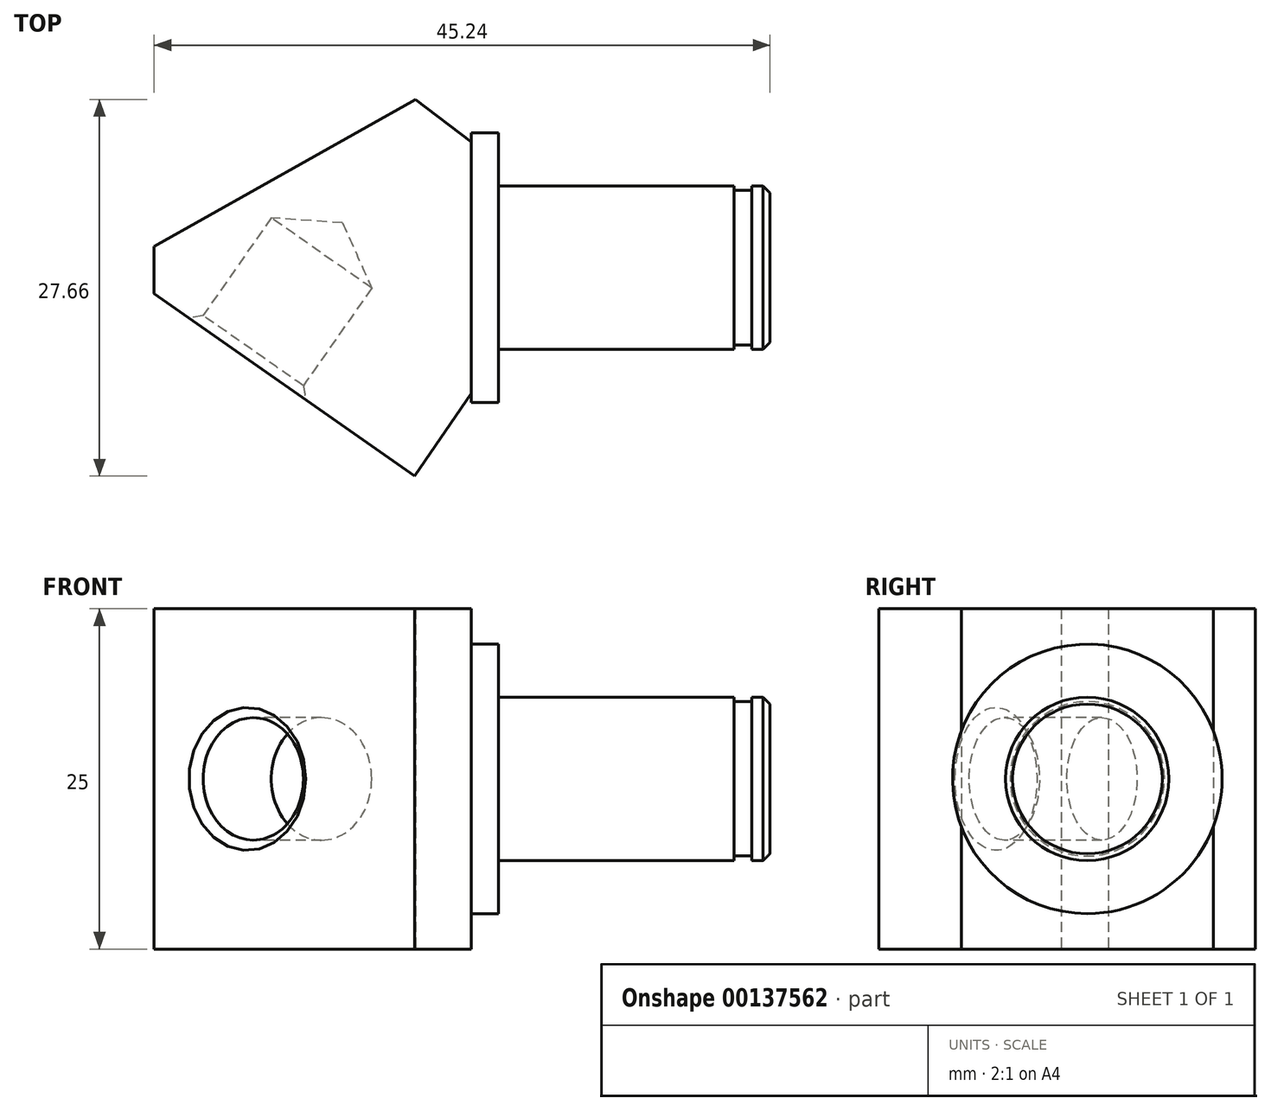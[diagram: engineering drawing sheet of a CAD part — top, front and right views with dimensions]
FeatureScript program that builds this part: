
annotation { "Feature Type Name" : "Feature", "Feature Type Description" : "" }
export const myFeature = defineFeature(function(context is Context, id is Id, definition is map)
    precondition{}
    {
        {
            var Q0;
            Q0=qCreatedBy(makeId("Top.planeOp"),FACE);
            var sketch = newSketch(context, id + "F0", { "sketchPlane" : qUnion([Q0])});
            skLineSegment(sketch, "E0", {"start": v(0, 9.25) * mm, "end": v(0, -9.25) * mm});
            skLineSegment(sketch, "E1", {"start": v(-4.1, 12.35) * mm, "end": v(-23.3, 1.54) * mm});
            skLineSegment(sketch, "E2", {"start": v(-23.3, -1.92) * mm, "end": v(-4.16, -15.3) * mm});
            skLineSegment(sketch, "E3", {"start": v(-26.04, 0) * mm, "end": v(0, 0) * mm, "construction": true});
            skLineSegment(sketch, "E4", {"start": v(-23.3, 1.54) * mm, "end": v(-23.3, -1.92) * mm});
            skPoint(sketch, "E5", {"position": v(-26.04, 0) * mm});
            skPoint(sketch, "E6", {"position": v(0, -18.22) * mm});
            skLineSegment(sketch, "E7", {"start": v(-23.3, -1.92) * mm, "end": v(-26.04, 0) * mm, "construction": true});
            skLineSegment(sketch, "E8", {"start": v(-23.3, 1.54) * mm, "end": v(-26.04, 0) * mm, "construction": true});
            skLineSegment(sketch, "E9", {"start": v(0, 9.25) * mm, "end": v(-4.1, 12.35) * mm});
            skLineSegment(sketch, "E10", {"start": v(0, 9.25) * mm, "end": v(0, 14.66) * mm, "construction": true});
            skLineSegment(sketch, "E11", {"start": v(0, 14.66) * mm, "end": v(-4.1, 12.35) * mm, "construction": true});
            skLineSegment(sketch, "E12", {"start": v(-4.16, -15.3) * mm, "end": v(0, -9.25) * mm});
            skLineSegment(sketch, "E13", {"start": v(0, -9.25) * mm, "end": v(0, -18.22) * mm, "construction": true});
            skLineSegment(sketch, "E14", {"start": v(-4.16, -15.3) * mm, "end": v(0, -18.22) * mm, "construction": true});
            skPoint(sketch, "E15", {"position": v(0, -20.34) * mm});
            skSolve(sketch);
        }
        {
            var Q0;
            Q0 = qSketchRegion(id + "F0", true);
            extrude(context, id + "F1", {"entities" : qUnion([Q0]), "endBound" : BoundingType.SYMMETRIC, "depth" : 25 * mm});
        }
        {
            var Q0;
            Q0=makeQuery(id+"F1.opExtrude","SWEPT_FACE",FACE,{"disambiguationData":[OSD([sQuery(id+"F0.wireOp",EDGE,"E2")])]});
            var sketch = newSketch(context, id + "F2", { "sketchPlane" : qUnion([Q0])});
            skCircle(sketch, "E16", {"center": v(-9.63, 0) * mm, "radius": 4.5 * mm});
            skSolve(sketch);
        }
        {
            var Q0;
            Q0=sQuery(id+"F2.wireOp",VERTEX,"E16.center");
            var Q1;
            Q1=makeQuery(id+"F1.opExtrude","SWEPT_BODY",BODY,{"disambiguationData":[OSD([sQuery(id+"F0.wireOp",EDGE,"E0"),sQuery(id+"F0.wireOp",EDGE,"E1"),sQuery(id+"F0.wireOp",EDGE,"E2"),sQuery(id+"F0.wireOp",EDGE,"E4"),sQuery(id+"F0.wireOp",EDGE,"E9"),sQuery(id+"F0.wireOp",EDGE,"E12")])]});
            hole(context, id + "F3", {"style" : HoleStyle.C_SINK, "endStyle" : HoleEndStyle.BLIND, "holeDiameter" : 9 * mm, "cSinkDiameter" : 10.5 * mm, "cSinkAngle" : 90 * degree, "holeDepth" : 9.5 * mm, "locations" : qUnion([Q0]), "scope" : qUnion([Q1])});
        }
        {
            var Q0;
            Q0=makeQuery(id+"F1.opExtrude","SWEPT_FACE",FACE,{"disambiguationData":[OSD([sQuery(id+"F0.wireOp",EDGE,"E0")])]});
            var sketch = newSketch(context, id + "F4", { "sketchPlane" : qUnion([Q0])});
            skCircle(sketch, "E17", {"center": v(0, 0) * mm, "radius": 9.9 * mm});
            skSolve(sketch);
        }
        {
            var Q0;
            Q0 = qSketchRegion(id + "F4", true);
            extrude(context, id + "F5", {"entities" : qUnion([Q0]), "operationType" : NewBodyOperationType.ADD, "depth" : 2 * mm});
        }
        {
            var Q0;
            Q0=makeQuery(id+"F5.opExtrude","CAP_FACE",FACE,{"disambiguationData":[OSD([sQuery(id+"F4.wireOp",EDGE,"E17")])],"isStart":false});
            var sketch = newSketch(context, id + "F6", { "sketchPlane" : qUnion([Q0])});
            skCircle(sketch, "E18", {"center": v(0, 0) * mm, "radius": 6 * mm});
            skSolve(sketch);
        }
        {
            var Q0;
            Q0 = qSketchRegion(id + "F6", true);
            extrude(context, id + "F7", {"entities" : qUnion([Q0]), "operationType" : NewBodyOperationType.ADD, "depth" : 17.3 * mm});
        }
        {
            var Q0;
            Q0=makeQuery(id+"F7.opExtrude","CAP_FACE",FACE,{"disambiguationData":[OSD([sQuery(id+"F6.wireOp",EDGE,"E18")])],"isStart":false});
            var sketch = newSketch(context, id + "F8", { "sketchPlane" : qUnion([Q0])});
            skCircle(sketch, "E19", {"center": v(0, 0) * mm, "radius": 5.67 * mm});
            skSolve(sketch);
        }
        {
            var Q0;
            Q0 = qSketchRegion(id + "F8", true);
            extrude(context, id + "F9", {"entities" : qUnion([Q0]), "operationType" : NewBodyOperationType.ADD, "depth" : 1.3 * mm});
        }
        {
            var Q0;
            Q0=makeQuery(id+"F9.opExtrude","CAP_FACE",FACE,{"disambiguationData":[OSD([sQuery(id+"F8.wireOp",EDGE,"E19")])],"isStart":false});
            var sketch = newSketch(context, id + "F10", { "sketchPlane" : qUnion([Q0])});
            skCircle(sketch, "E20", {"center": v(0, 0) * mm, "radius": 6 * mm});
            skSolve(sketch);
        }
        {
            var Q0;
            Q0 = qSketchRegion(id + "F10", true);
            extrude(context, id + "F11", {"entities" : qUnion([Q0]), "operationType" : NewBodyOperationType.ADD, "depth" : 1.34 * mm});
        }
        {
            var Q0;
            Q0=makeQuery(id+"F11.opExtrude","CAP_EDGE",EDGE,{"disambiguationData":[OSD([sQuery(id+"F10.wireOp",EDGE,"E20")])],"isStart":false});
            chamfer(context, id + "F12", {"entities" : qUnion([Q0]), "width" : 0.5 * mm, "tangentPropagation" : true});
        }
    });
